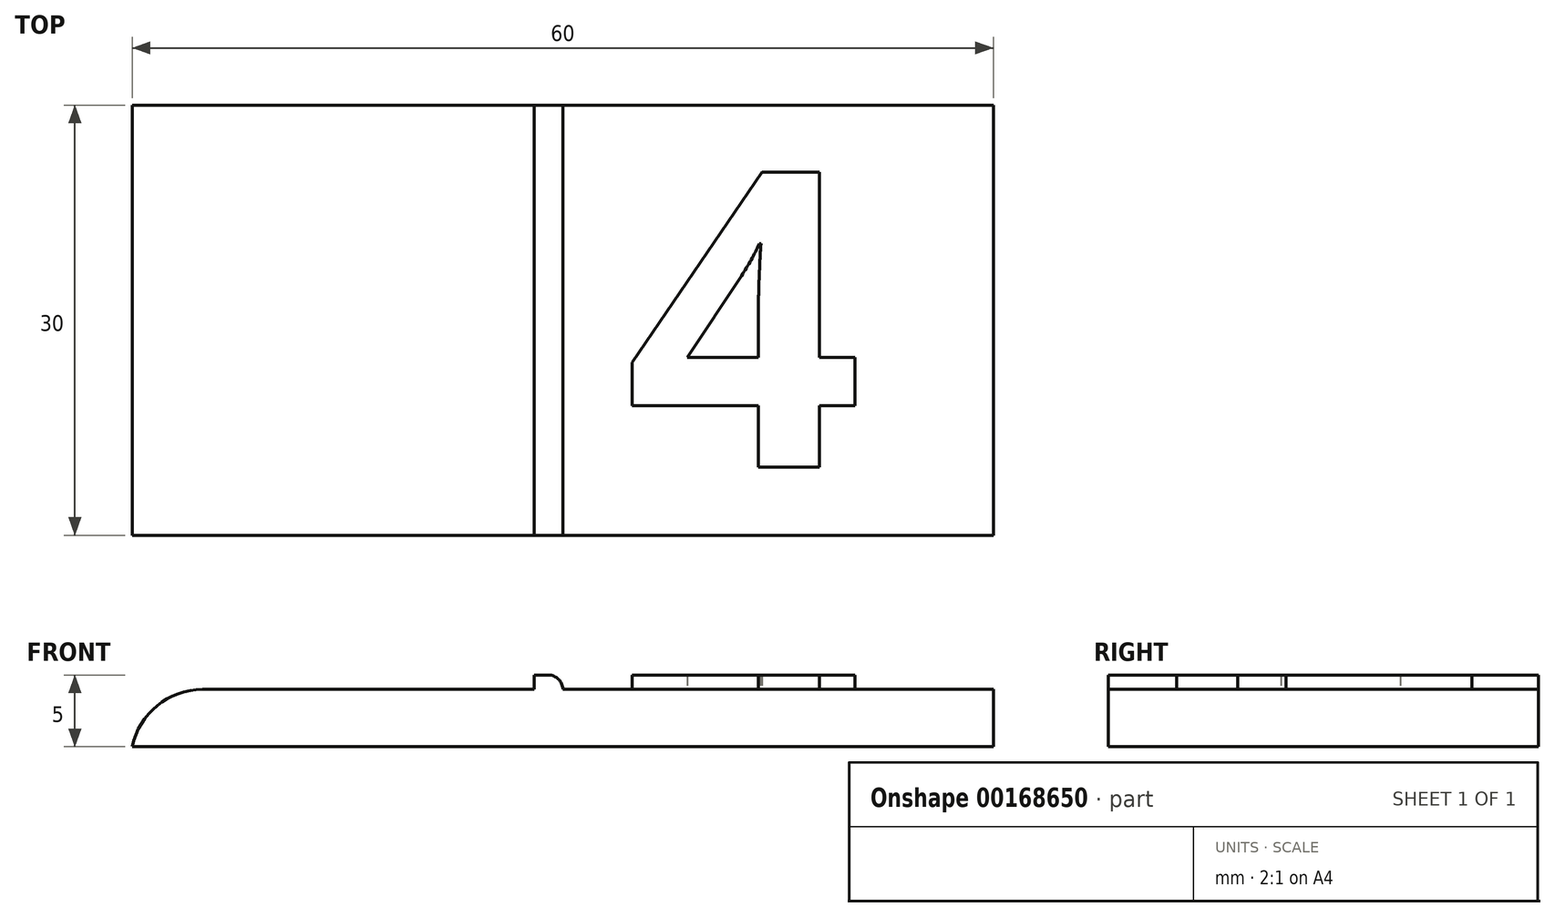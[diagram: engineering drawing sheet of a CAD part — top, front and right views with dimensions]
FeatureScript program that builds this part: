
annotation { "Feature Type Name" : "Feature", "Feature Type Description" : "" }
export const myFeature = defineFeature(function(context is Context, id is Id, definition is map)
    precondition{}
    {
        {
            var Q0;
            Q0=qCreatedBy(makeId("Top.planeOp"),FACE);
            var sketch = newSketch(context, id + "F0", { "sketchPlane" : qUnion([Q0])});
            skLineSegment(sketch, "E0.bottom", {"start": v(0, 0) * mm, "end": v(60, 0) * mm});
            skLineSegment(sketch, "E0.top", {"start": v(0, 30) * mm, "end": v(60, 30) * mm});
            skLineSegment(sketch, "E0.left", {"start": v(0, 0) * mm, "end": v(0, 30) * mm});
            skLineSegment(sketch, "E0.right", {"start": v(60, 0) * mm, "end": v(60, 30) * mm});
            skSolve(sketch);
        }
        {
            var Q0;
            Q0=qSketchRegion(id+"F0",true);
            extrude(context, id + "F1", {"entities" : qUnion([Q0]), "depth" : 4 * mm});
        }
        {
            var Q0;
            Q0=makeQuery(id+"F1.opExtrude","CAP_FACE",FACE,{"disambiguationData":[OSD([sQuery(id+"F0.wireOp",EDGE,"E0.bottom"),sQuery(id+"F0.wireOp",EDGE,"E0.top"),sQuery(id+"F0.wireOp",EDGE,"E0.left"),sQuery(id+"F0.wireOp",EDGE,"E0.right")])],"isStart":false});
            var sketch = newSketch(context, id + "F2", { "sketchPlane" : qUnion([Q0])});
            skLineSegment(sketch, "E1.bottom", {"start": v(30, 30) * mm, "end": v(28, 30) * mm});
            skLineSegment(sketch, "E1.top", {"start": v(30, 0) * mm, "end": v(28, 0) * mm});
            skLineSegment(sketch, "E1.left", {"start": v(30, 30) * mm, "end": v(30, 0) * mm});
            skLineSegment(sketch, "E1.right", {"start": v(28, 30) * mm, "end": v(28, 0) * mm});
            skSolve(sketch);
        }
        {
            var Q0;
            Q0=qSketchRegion(id+"F2",true);
            extrude(context, id + "F3", {"entities" : qUnion([Q0]), "operationType" : NewBodyOperationType.ADD, "depth" : 1 * mm});
        }
        {
            var Q0;
            Q0=makeQuery(id+"F3.opExtrude","CAP_EDGE",EDGE,{"disambiguationData":[OSD([sQuery(id+"F2.wireOp",EDGE,"E1.left")])],"isStart":false});
            fillet(context, id + "F4", {"entities" : qUnion([Q0]), "radius" : 1 * mm, "tangentPropagation" : true, "allowEdgeOverflow" : false});
        }
        {
            var Q0;
            {var subQ0=sQuery(id+"F0.wireOp",EDGE,"E0.top");var subQ1=sQuery(id+"F0.wireOp",EDGE,"E0.right");var subQ2=sQuery(id+"F0.wireOp",EDGE,"E0.bottom");Q0=makeQuery(id+"F3.boolean.opBoolean","SPLIT",FACE,{"disambiguationData":[TD([makeQuery(id+"F1.opExtrude","SWEPT_FACE",FACE,{"disambiguationData":[OSD([subQ1])]})])],"derivedFrom":makeQuery(id+"F1.opExtrude","CAP_FACE",FACE,{"disambiguationData":[OSD([subQ2,subQ0,sQuery(id+"F0.wireOp",EDGE,"E0.left"),subQ1])],"isStart":false})});}
            var sketch = newSketch(context, id + "F5", { "sketchPlane" : qUnion([Q0])});
            skText(sketch, "E2", { "text": "4", "fontName": "OpenSans-Bold.ttf"});
            const initialGuessF5  = {"E2": [0.03436, 0.00476, 1, 0, 0.02075]};
            skSetInitialGuess(sketch, initialGuessF5);
            skSolve(sketch);
        }
        {
            var Q0;
            Q0=qSketchRegion(id+"F5",true);
            extrude(context, id + "F6", {"entities" : qUnion([Q0]), "operationType" : NewBodyOperationType.ADD, "depth" : 1 * mm});
        }
        {
            var Q0;
            Q0=makeQuery(id+"F1.opExtrude","CAP_EDGE",EDGE,{"disambiguationData":[OSD([sQuery(id+"F0.wireOp",EDGE,"E0.left")])],"isStart":false});
            fillet(context, id + "F7", {"entities" : qUnion([Q0]), "radius" : 5 * mm, "tangentPropagation" : true, "allowEdgeOverflow" : false});
        }
    });
